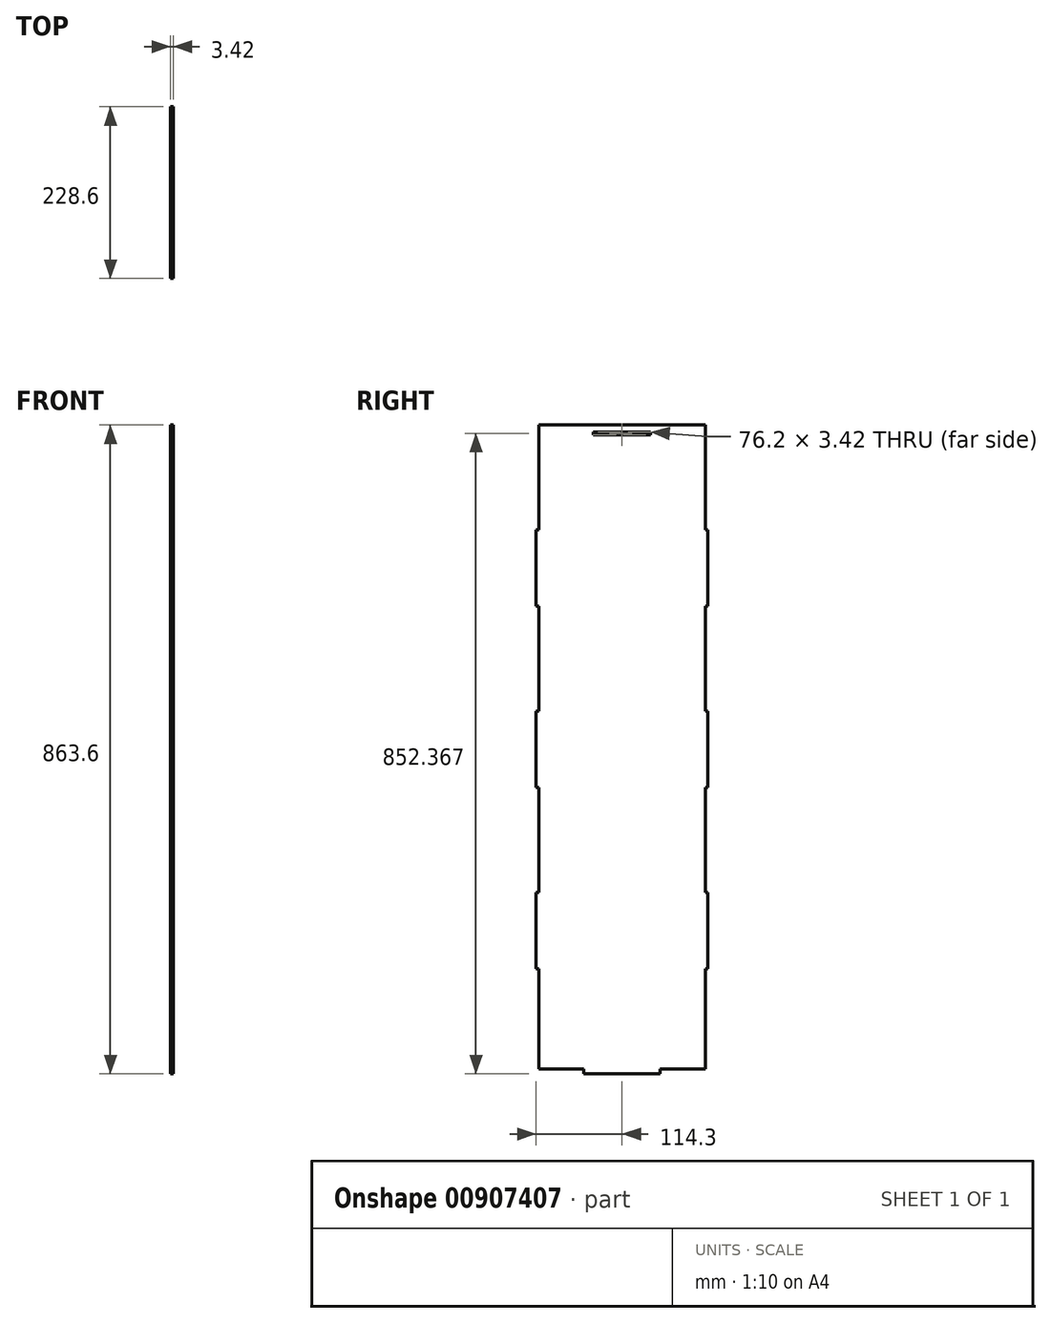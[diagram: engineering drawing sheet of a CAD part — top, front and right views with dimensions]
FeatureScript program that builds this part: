
annotation { "Feature Type Name" : "Feature", "Feature Type Description" : "" }
export const myFeature = defineFeature(function(context is Context, id is Id, definition is map)
    precondition{}
    {
        {
            var Q0;
            Q0=qCreatedBy(makeId("Right.planeOp"),FACE);
            var sketch = newSketch(context, id + "F0", { "sketchPlane" : qUnion([Q0])});
            skLineSegment(sketch, "E0", {"start": v(-50.8, -6.35) * mm, "end": v(50.8, -6.35) * mm});
            skLineSegment(sketch, "E1", {"start": v(50.8, -6.35) * mm, "end": v(50.8, 0) * mm});
            skLineSegment(sketch, "E2", {"start": v(-50.8, -6.35) * mm, "end": v(-50.8, 0) * mm});
            skLineSegment(sketch, "E3", {"start": v(-50.8, 0) * mm, "end": v(-110.88, 0) * mm});
            skLineSegment(sketch, "E4", {"start": v(-110.88, 0) * mm, "end": v(-110.88, 133.35) * mm});
            skLineSegment(sketch, "E5", {"start": v(-110.88, 133.35) * mm, "end": v(-114.3, 133.35) * mm});
            skLineSegment(sketch, "E6", {"start": v(-114.3, 133.35) * mm, "end": v(-114.3, 234.95) * mm});
            skLineSegment(sketch, "E7", {"start": v(-114.3, 234.95) * mm, "end": v(-110.88, 234.95) * mm});
            skLineSegment(sketch, "E8", {"start": v(-110.88, 234.95) * mm, "end": v(-110.88, 374.65) * mm});
            skLineSegment(sketch, "E9", {"start": v(-110.88, 374.65) * mm, "end": v(-114.3, 374.65) * mm});
            skLineSegment(sketch, "E10", {"start": v(-114.3, 374.65) * mm, "end": v(-114.3, 476.25) * mm});
            skLineSegment(sketch, "E11", {"start": v(-114.3, 476.25) * mm, "end": v(-110.88, 476.25) * mm});
            skLineSegment(sketch, "E12", {"start": v(-110.88, 476.25) * mm, "end": v(-110.88, 615.95) * mm});
            skLineSegment(sketch, "E13", {"start": v(-110.88, 615.95) * mm, "end": v(-114.3, 615.95) * mm});
            skLineSegment(sketch, "E14", {"start": v(-114.3, 615.95) * mm, "end": v(-114.3, 717.55) * mm});
            skLineSegment(sketch, "E15", {"start": v(-114.3, 717.55) * mm, "end": v(-110.88, 717.55) * mm});
            skLineSegment(sketch, "E16", {"start": v(50.8, 0) * mm, "end": v(110.88, 0) * mm});
            skLineSegment(sketch, "E17", {"start": v(-110.88, 717.55) * mm, "end": v(-110.88, 857.25) * mm});
            skLineSegment(sketch, "E18", {"start": v(-110.88, 857.25) * mm, "end": v(-38.1, 857.25) * mm});
            skLineSegment(sketch, "E19", {"start": v(-38.1, 847.72) * mm, "end": v(-38.1, 844.3) * mm});
            skLineSegment(sketch, "E20", {"start": v(-38.1, 844.3) * mm, "end": v(38.1, 844.3) * mm});
            skLineSegment(sketch, "E21", {"start": v(38.1, 844.3) * mm, "end": v(38.1, 847.72) * mm});
            skLineSegment(sketch, "E22", {"start": v(38.1, 857.25) * mm, "end": v(110.88, 857.25) * mm});
            skLineSegment(sketch, "E23", {"start": v(0, 844.3) * mm, "end": v(0, 0) * mm, "construction": true});
            skLineSegment(sketch, "E24.MirrorCS", {"start": v(110.88, 374.65) * mm, "end": v(114.3, 374.65) * mm});
            skLineSegment(sketch, "E25.MirrorCS", {"start": v(110.88, 615.95) * mm, "end": v(114.3, 615.95) * mm});
            skLineSegment(sketch, "E26.MirrorCS", {"start": v(110.88, 133.35) * mm, "end": v(114.3, 133.35) * mm});
            skLineSegment(sketch, "E27.MirrorCS", {"start": v(114.3, 476.25) * mm, "end": v(110.88, 476.25) * mm});
            skLineSegment(sketch, "E28.MirrorCS", {"start": v(114.3, 234.95) * mm, "end": v(110.88, 234.95) * mm});
            skLineSegment(sketch, "E29.MirrorCS", {"start": v(114.3, 717.55) * mm, "end": v(110.88, 717.55) * mm});
            skLineSegment(sketch, "E30.MirrorCS", {"start": v(110.88, 476.25) * mm, "end": v(110.88, 615.95) * mm});
            skLineSegment(sketch, "E31.MirrorCS", {"start": v(110.88, 234.95) * mm, "end": v(110.88, 374.65) * mm});
            skLineSegment(sketch, "E32.MirrorCS", {"start": v(110.88, 717.55) * mm, "end": v(110.88, 857.25) * mm});
            skLineSegment(sketch, "E33.MirrorCS", {"start": v(114.3, 374.65) * mm, "end": v(114.3, 476.25) * mm});
            skLineSegment(sketch, "E34.MirrorCS", {"start": v(114.3, 133.35) * mm, "end": v(114.3, 234.95) * mm});
            skLineSegment(sketch, "E35.MirrorCS", {"start": v(110.88, 0) * mm, "end": v(110.88, 133.35) * mm});
            skLineSegment(sketch, "E36.MirrorCS", {"start": v(114.3, 615.95) * mm, "end": v(114.3, 717.55) * mm});
            skLineSegment(sketch, "E37", {"start": v(-38.1, 857.25) * mm, "end": v(38.1, 857.25) * mm});
            skLineSegment(sketch, "E38.0", {"start": v(-38.1, 847.72) * mm, "end": v(38.1, 847.72) * mm});
            skSolve(sketch);
        }
        {
            var Q0;
            Q0 = qSketchRegion(id + "F0", true);
            extrude(context, id + "F1", {"entities" : qUnion([Q0]), "depth" : 3.42 * mm, "offsetDistance" : 25.4 * mm});
        }
    });
